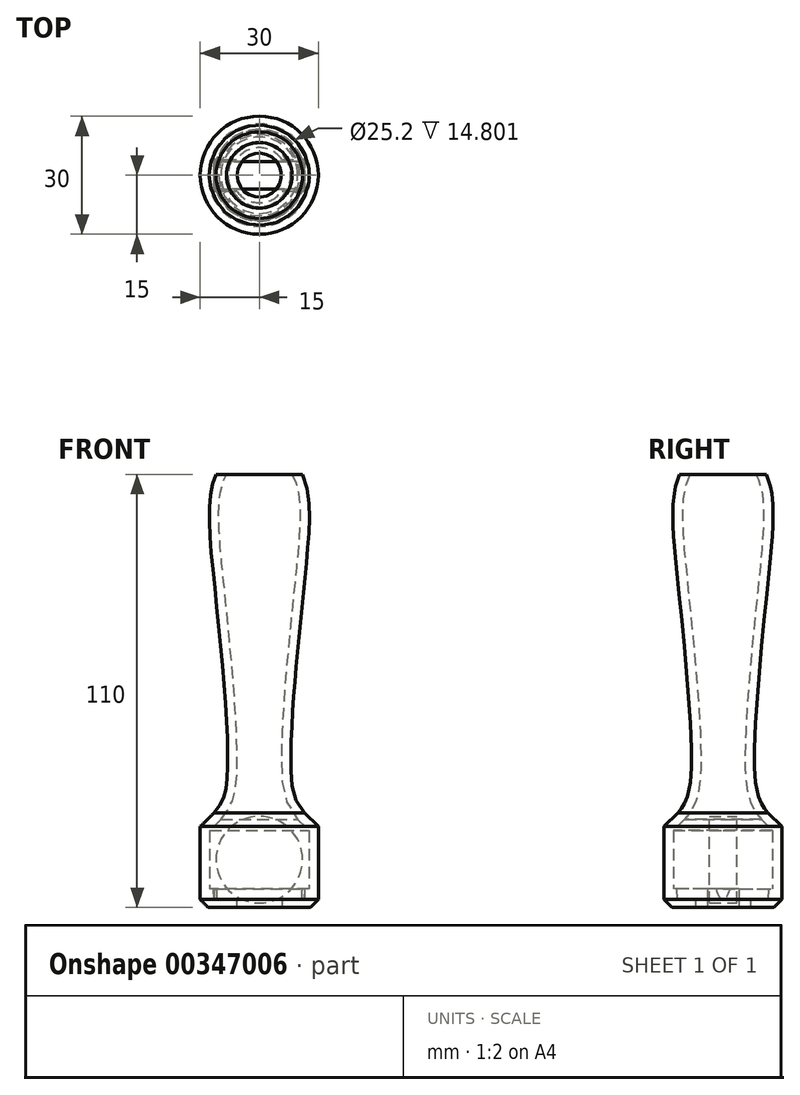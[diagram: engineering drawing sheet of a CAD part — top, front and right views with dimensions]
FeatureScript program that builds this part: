
annotation { "Feature Type Name" : "Feature", "Feature Type Description" : "" }
export const myFeature = defineFeature(function(context is Context, id is Id, definition is map)
    precondition{}
    {
        {
            var Q0;
            Q0=qCreatedBy(makeId("Front.planeOp"),FACE);
            var sketch = newSketch(context, id + "F0", { "sketchPlane" : qUnion([Q0])});
            skLineSegment(sketch, "E0", {"start": v(0, 0) * mm, "end": v(0, 22.52) * mm});
            skLineSegment(sketch, "E1", {"start": v(0, 22.52) * mm, "end": v(0, 110) * mm});
            skLineSegment(sketch, "E2", {"start": v(11, 110) * mm, "end": v(0, 110) * mm});
            skLineSegment(sketch, "E3", {"start": v(28.07, 0) * mm, "end": v(28.07, 22) * mm});
            skLineSegment(sketch, "E4", {"start": v(0, 0) * mm, "end": v(13, 0) * mm});
            skLineSegment(sketch, "E5", {"start": v(13, 0) * mm, "end": v(15, 2) * mm});
            skLineSegment(sketch, "E6", {"start": v(15, 2) * mm, "end": v(15, 20.5) * mm});
            skLineSegment(sketch, "E7", {"start": v(15, 20.5) * mm, "end": v(11.46, 24.04) * mm});
            skFitSpline(sketch, "E8", {"points": [v(11.46, 24.04) * mm, v(8, 37) * mm, v(11.46, 82.68) * mm, v(11, 110) * mm], "startDerivative": vector(-36.59, 39.16) * mm, "endDerivative": vector(-24.54, 51.12) * mm});
            skSolve(sketch);
        }
        {
            var Q0;
            Q0=makeQuery(id+"F0.imprint","IMPRINT",FACE,{"disambiguationData":[TD([[makeQuery(id+"F0.imprint","IMPRINT",EDGE,{"derivedFrom":sQuery(id+"F0.wireOp",EDGE,"E0")}),-1.0]])]});
            var Q1;
            Q1=sQuery(id+"F0.wireOp",EDGE,"E0");
            revolve(context, id + "F1", {"entities" : qUnion([Q0]), "axis" : qUnion([Q1]), "revolveType" : RevolveType.FULL});
        }
        {
            var Q0;
            Q0=makeQuery(id+"F1.opRevolve","SWEPT_FACE",FACE,{"disambiguationData":[OSD([sQuery(id+"F0.wireOp",EDGE,"E2")])]});
            shell(context, id + "F2", {"entities" : qUnion([Q0]), "thickness" : 2.4 * mm});
        }
        {
            var Q0;
            Q0=qCreatedBy(makeId("Top.planeOp"),FACE);
            var sketch = newSketch(context, id + "F3", { "sketchPlane" : qUnion([Q0])});
            skCircle(sketch, "E9", {"center": v(0, 0) * mm, "radius": 7 * mm});
            skSolve(sketch);
        }
        {
            var Q0;
            Q0=makeQuery(id+"F3.imprint","IMPRINT",FACE,{"disambiguationData":[TD([[makeQuery(id+"F3.imprint","IMPRINT",EDGE,{"derivedFrom":sQuery(id+"F3.wireOp",EDGE,"E9")}),1.0]])]});
            extrude(context, id + "F4", {"entities" : qUnion([Q0]), "operationType" : NewBodyOperationType.REMOVE, "depth" : 13.2 * mm});
        }
        {
            var Q0;
            Q0=qCreatedBy(makeId("Front.planeOp"),FACE);
            var sketch = newSketch(context, id + "F5", { "sketchPlane" : qUnion([Q0])});
            skCircle(sketch, "E10", {"center": v(0, 12.1) * mm, "radius": 11 * mm});
            skSolve(sketch);
        }
        {
            var Q0;
            Q0=qCreatedBy(makeId("Top.planeOp"),FACE);
            var sketch = newSketch(context, id + "F6", { "sketchPlane" : qUnion([Q0])});
            skLineSegment(sketch, "E11.bottom", {"start": v(-11.5, -4) * mm, "end": v(11.5, -4) * mm});
            skLineSegment(sketch, "E11.top", {"start": v(-11.5, 4) * mm, "end": v(11.5, 4) * mm});
            skLineSegment(sketch, "E11.left", {"start": v(-11.5, -4) * mm, "end": v(-11.5, 4) * mm});
            skLineSegment(sketch, "E11.right", {"start": v(11.5, -4) * mm, "end": v(11.5, 4) * mm});
            skPoint(sketch, "E12", {"position": v(0, -4) * mm});
            skPoint(sketch, "E13", {"position": v(11.5, 0) * mm});
            skSolve(sketch);
        }
        {
            var Q0;
            Q0=qCreatedBy(makeId("Top.planeOp"),FACE);
            cPlane(context, id + "F7", {"entities" : qUnion([Q0]), "cplaneType" : CPlaneType.OFFSET, "offset" : 2 * mm, "width" : 150 * mm, "height" : 150 * mm});
        }
        {
            var Q0;
            Q0=qCreatedBy(id+"F7.planeOp",FACE);
            var sketch = newSketch(context, id + "F8", { "sketchPlane" : qUnion([Q0])});
            skCircle(sketch, "E14", {"center": v(0, 0) * mm, "radius": 12.65 * mm});
            skSolve(sketch);
        }
        {
            var Q0;
            Q0 = qSketchRegion(id + "F8", true);
            extrude(context, id + "F9", {"entities" : qUnion([Q0]), "operationType" : NewBodyOperationType.ADD, "depth" : 2.7 * mm});
        }
        {
            var Q0;
            Q0=qCreatedBy(id+"F7.planeOp",FACE);
            var sketch = newSketch(context, id + "F10", { "sketchPlane" : qUnion([Q0])});
            skCircle(sketch, "E15", {"center": v(0, 0) * mm, "radius": 11.5 * mm});
            skSolve(sketch);
        }
        {
            var Q0;
            Q0 = qSketchRegion(id + "F6", true);
            var Q1;
            Q1=makeQuery(id+"F2.opShell","OFFSET_FACE",FACE,{"disambiguationData":[OSD([sQuery(id+"F0.wireOp",EDGE,"E4")])]});
            extrude(context, id + "F11", {"entities" : qUnion([Q0]), "operationType" : NewBodyOperationType.REMOVE, "endBoundEntityFace" : qUnion([Q1]), "depth" : 15 * mm});
        }
        {
            var Q0;
            Q0 = qSketchRegion(id + "F10", true);
            extrude(context, id + "F12", {"entities" : qUnion([Q0]), "operationType" : NewBodyOperationType.REMOVE, "depth" : 4 * mm, "hasDraft" : true, "draftAngle" : 3 * degree});
        }
        {
            var Q0;
            Q0=makeQuery(id+"F5.imprint","IMPRINT",FACE,{"disambiguationData":[TD([[makeQuery(id+"F5.imprint","IMPRINT",EDGE,{"derivedFrom":sQuery(id+"F5.wireOp",EDGE,"E10")}),1.0]])]});
            extrude(context, id + "F13", {"entities" : qUnion([Q0]), "endBound" : BoundingType.SYMMETRIC, "depth" : 7 * mm});
        }
        {
            var Q0;
            Q0=qCreatedBy(makeId("Right.planeOp"),FACE);
            cPlane(context, id + "F14", {"entities" : qUnion([Q0]), "cplaneType" : CPlaneType.OFFSET, "offset" : 50 * mm, "width" : 150 * mm, "height" : 150 * mm});
        }
    });
